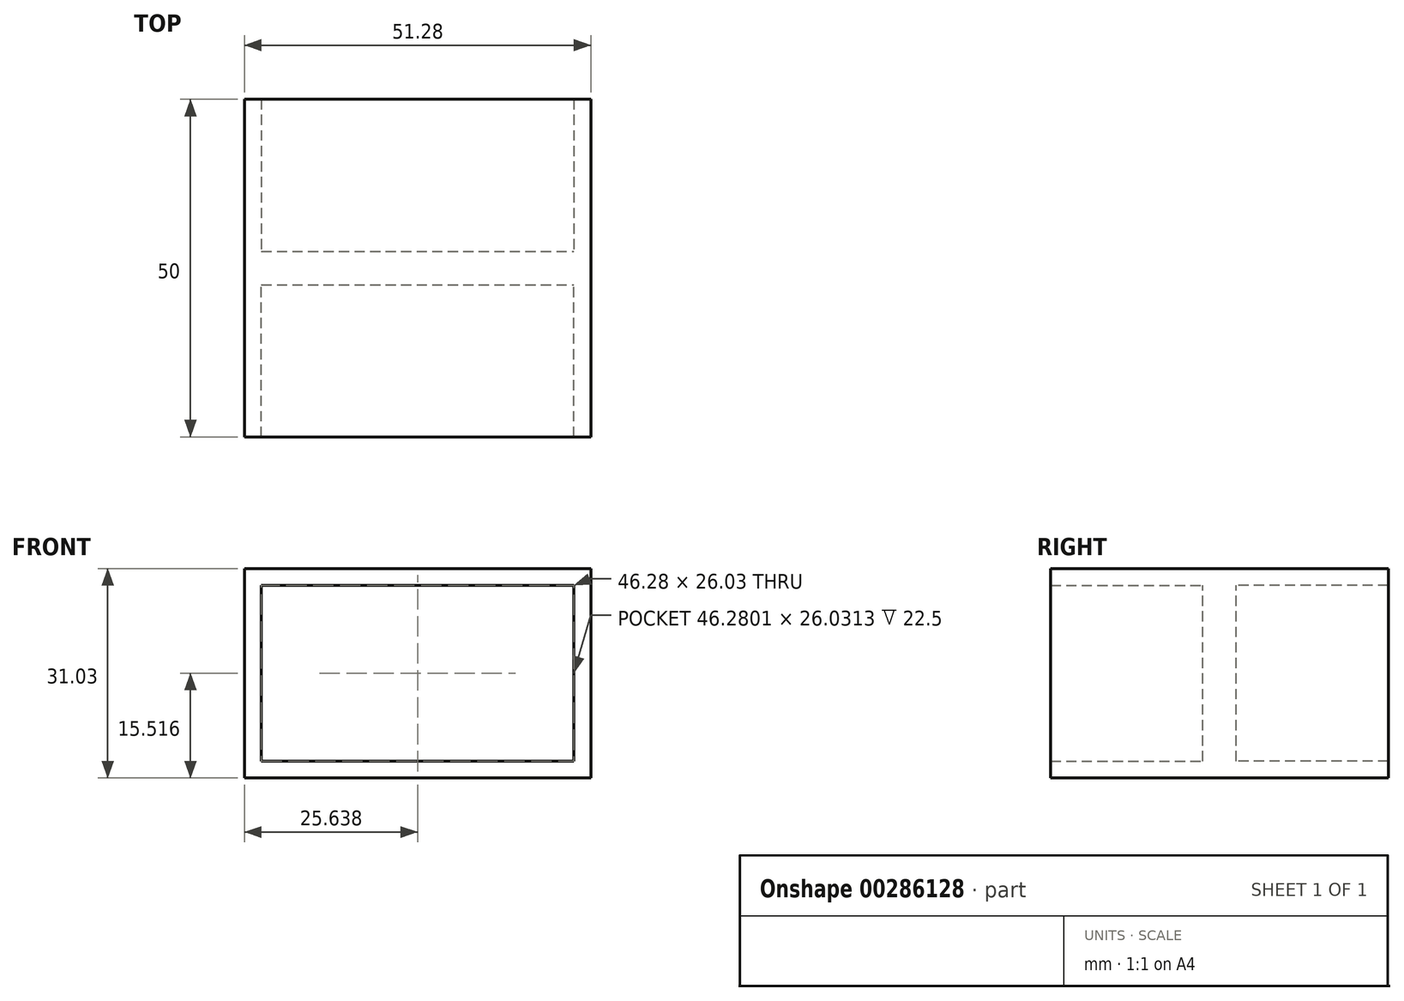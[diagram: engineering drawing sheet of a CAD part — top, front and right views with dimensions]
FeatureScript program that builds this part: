
annotation { "Feature Type Name" : "Feature", "Feature Type Description" : "" }
export const myFeature = defineFeature(function(context is Context, id is Id, definition is map)
    precondition{}
    {
        {
            var Q0;
            Q0=qCreatedBy(makeId("Front.planeOp"),FACE);
            var sketch = newSketch(context, id + "F0", { "sketchPlane" : qUnion([Q0])});
            skLineSegment(sketch, "E0.bottom", {"start": v(-75.62, 28.8) * mm, "end": v(-24.34, 28.8) * mm});
            skLineSegment(sketch, "E0.top", {"start": v(-75.62, 59.83) * mm, "end": v(-24.34, 59.83) * mm});
            skLineSegment(sketch, "E0.left", {"start": v(-75.62, 28.8) * mm, "end": v(-75.62, 59.83) * mm});
            skLineSegment(sketch, "E0.right", {"start": v(-24.34, 28.8) * mm, "end": v(-24.34, 59.83) * mm});
            skPoint(sketch, "E0.middle", {"position": v(-49.98, 44.32) * mm});
            skSolve(sketch);
        }
        {
            var Q0;
            Q0=makeQuery(id+"F0.imprint","IMPRINT",FACE,{"disambiguationData":[TD([[makeQuery(id+"F0.imprint","IMPRINT",EDGE,{"derivedFrom":sQuery(id+"F0.wireOp",EDGE,"E0.bottom")}),1.0]])]});
            extrude(context, id + "F1", {"entities" : qUnion([Q0]), "depth" : 25 * mm});
        }
        {
            var Q0;
            Q0=makeQuery(id+"F1.opExtrude","CAP_FACE",FACE,{"disambiguationData":[OSD([sQuery(id+"F0.wireOp",EDGE,"E0.bottom"),sQuery(id+"F0.wireOp",EDGE,"E0.top"),sQuery(id+"F0.wireOp",EDGE,"E0.left"),sQuery(id+"F0.wireOp",EDGE,"E0.right")])],"isStart":false});
            shell(context, id + "F2", {"entities" : qUnion([Q0]), "thickness" : 2.5 * mm});
        }
        {
            var Q0;
            Q0=makeQuery(id+"F1.opExtrude","SWEPT_BODY",BODY,{"disambiguationData":[OSD([sQuery(id+"F0.wireOp",EDGE,"E0.bottom"),sQuery(id+"F0.wireOp",EDGE,"E0.top"),sQuery(id+"F0.wireOp",EDGE,"E0.left"),sQuery(id+"F0.wireOp",EDGE,"E0.right")])]});
            var Q1;
            Q1=makeQuery(id+"F1.opExtrude","CAP_FACE",FACE,{"disambiguationData":[OSD([sQuery(id+"F0.wireOp",EDGE,"E0.bottom"),sQuery(id+"F0.wireOp",EDGE,"E0.top"),sQuery(id+"F0.wireOp",EDGE,"E0.left"),sQuery(id+"F0.wireOp",EDGE,"E0.right")])],"isStart":true});
            mirror(context, id + "F3", {"operationType" : NewBodyOperationType.ADD, "entities" : qUnion([Q0]), "mirrorPlane" : qUnion([Q1])});
        }
    });
